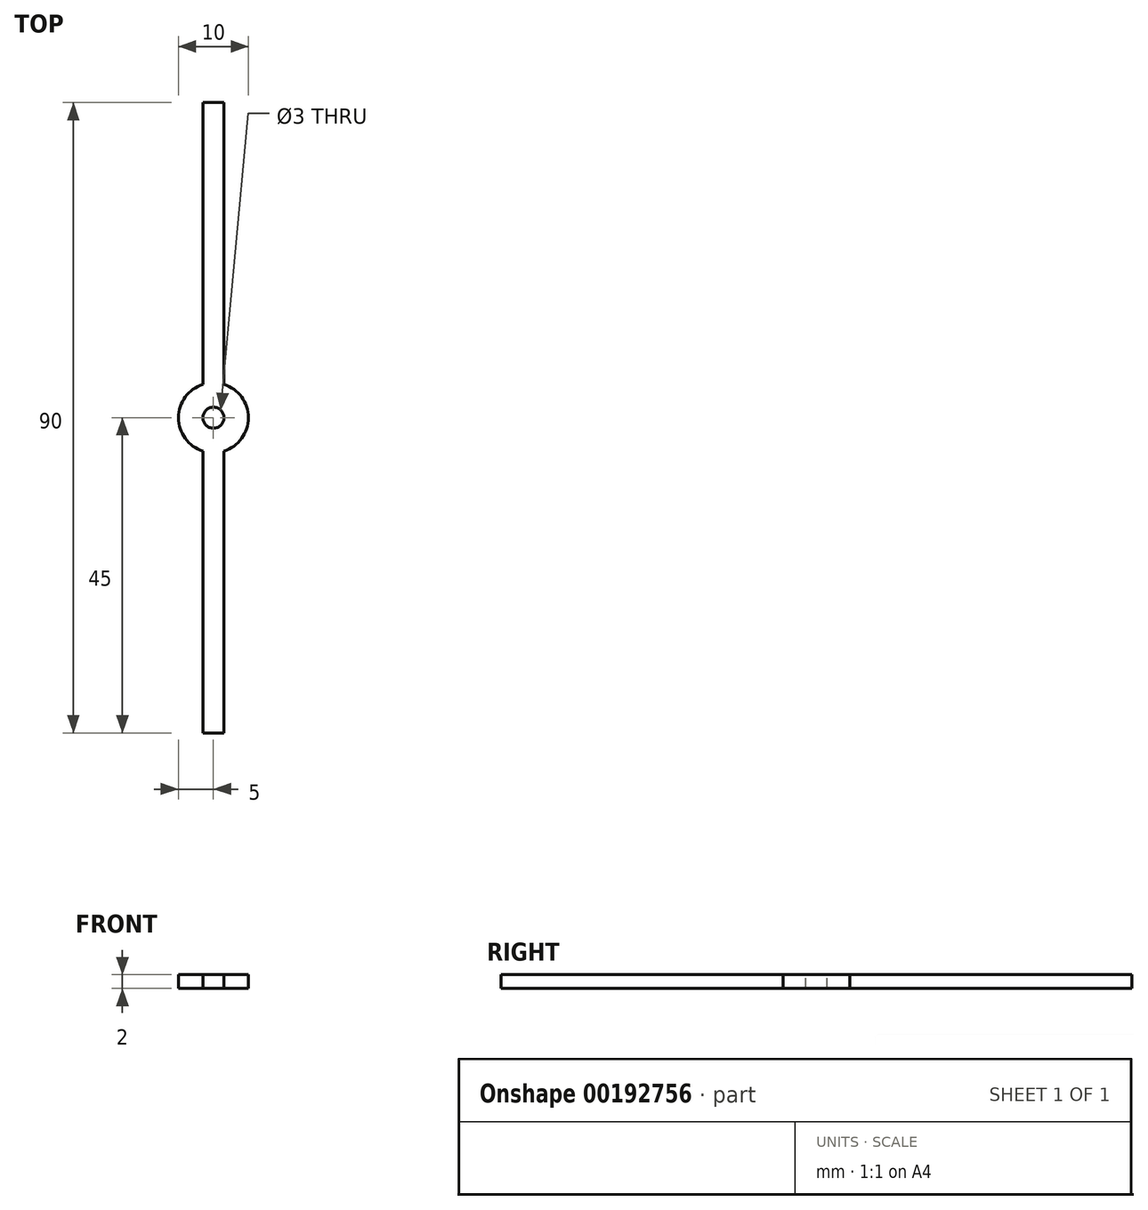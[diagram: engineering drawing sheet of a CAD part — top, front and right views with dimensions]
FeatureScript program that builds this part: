
annotation { "Feature Type Name" : "Feature", "Feature Type Description" : "" }
export const myFeature = defineFeature(function(context is Context, id is Id, definition is map)
    precondition{}
    {
        {
            var Q0;
            Q0=qCreatedBy(makeId("Top.planeOp"),FACE);
            var sketch = newSketch(context, id + "F0", { "sketchPlane" : qUnion([Q0])});
            skCircle(sketch, "E0", {"center": v(0, 0) * mm, "radius": 5 * mm});
            skLineSegment(sketch, "E1", {"start": v(0, 0) * mm, "end": v(0, 5) * mm, "construction": true});
            skLineSegment(sketch, "E2", {"start": v(0, 5) * mm, "end": v(0, 45) * mm});
            skLineSegment(sketch, "E3", {"start": v(0, 45) * mm, "end": v(-1.5, 45) * mm});
            skLineSegment(sketch, "E4", {"start": v(-1.5, 45) * mm, "end": v(-1.5, 4.77) * mm});
            skLineSegment(sketch, "E5.MirrorCS", {"start": v(0, 45) * mm, "end": v(1.5, 45) * mm});
            skLineSegment(sketch, "E6.MirrorCS", {"start": v(1.5, 45) * mm, "end": v(1.5, 4.77) * mm});
            skLineSegment(sketch, "E7.1.0", {"start": v(-1.5, -45) * mm, "end": v(-1.5, -4.77) * mm});
            skLineSegment(sketch, "E7.1.1", {"start": v(0, -45) * mm, "end": v(-1.5, -45) * mm});
            skLineSegment(sketch, "E7.1.2", {"start": v(0, -45) * mm, "end": v(1.5, -45) * mm});
            skLineSegment(sketch, "E7.1.3", {"start": v(1.5, -45) * mm, "end": v(1.5, -4.77) * mm});
            skSolve(sketch);
        }
        {
            var Q0;
            Q0 = qSketchRegion(id + "F0", true);
            extrude(context, id + "F1", {"entities" : qUnion([Q0]), "depth" : 2 * mm});
        }
        {
            var Q0;
            Q0=makeQuery(id+"F1.opExtrude","CAP_FACE",FACE,{"disambiguationData":[OSD([sQuery(id+"F0.wireOp",EDGE,"E0"),sQuery(id+"F0.wireOp",EDGE,"E3"),sQuery(id+"F0.wireOp",EDGE,"E4"),sQuery(id+"F0.wireOp",EDGE,"E5.MirrorCS"),sQuery(id+"F0.wireOp",EDGE,"E6.MirrorCS"),sQuery(id+"F0.wireOp",EDGE,"E7.1.0"),sQuery(id+"F0.wireOp",EDGE,"E7.1.1"),sQuery(id+"F0.wireOp",EDGE,"E7.1.2"),sQuery(id+"F0.wireOp",EDGE,"E7.1.3")])],"isStart":false});
            var sketch = newSketch(context, id + "F2", { "sketchPlane" : qUnion([Q0])});
            skCircle(sketch, "E8", {"center": v(0, 0) * mm, "radius": 1.5 * mm});
            skSolve(sketch);
        }
        {
            var Q0;
            Q0 = qSketchRegion(id + "F2", true);
            extrude(context, id + "F3", {"entities" : qUnion([Q0]), "operationType" : NewBodyOperationType.REMOVE, "oppositeDirection" : true, "depth" : 25 * mm});
        }
    });
